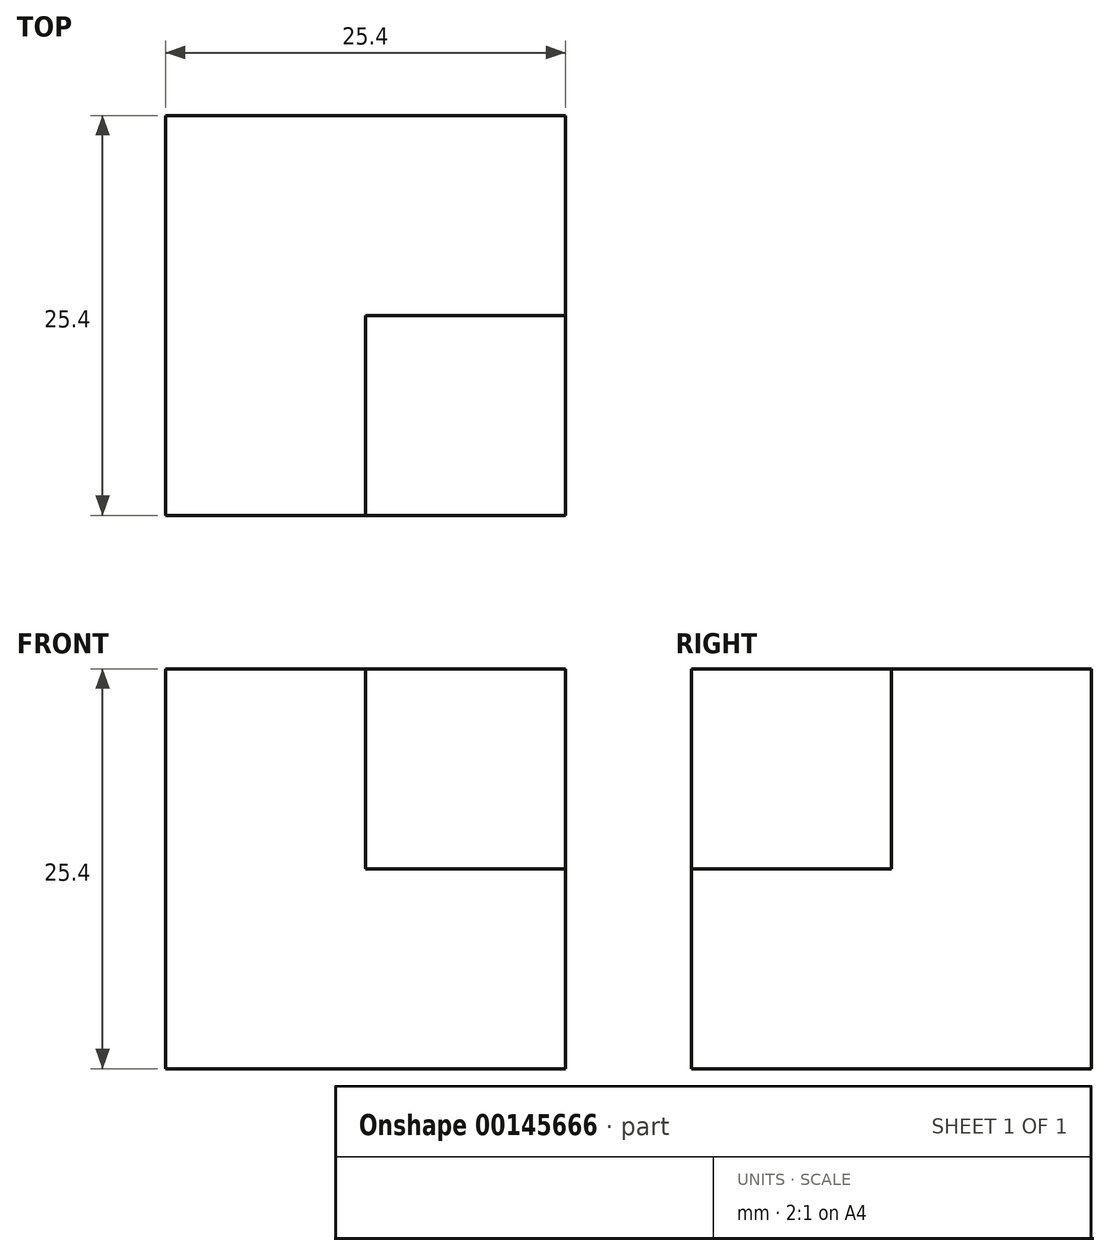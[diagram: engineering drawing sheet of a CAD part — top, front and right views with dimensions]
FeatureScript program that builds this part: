
annotation { "Feature Type Name" : "Feature", "Feature Type Description" : "" }
export const myFeature = defineFeature(function(context is Context, id is Id, definition is map)
    precondition{}
    {
        {
            var Q0;
            Q0=qCreatedBy(makeId("Top.planeOp"),FACE);
            var sketch = newSketch(context, id + "F0", { "sketchPlane" : qUnion([Q0])});
            skLineSegment(sketch, "E0.bottom", {"start": v(12.7, -12.7) * mm, "end": v(-12.7, -12.7) * mm});
            skLineSegment(sketch, "E0.top", {"start": v(12.7, 12.7) * mm, "end": v(-12.7, 12.7) * mm});
            skLineSegment(sketch, "E0.left", {"start": v(12.7, -12.7) * mm, "end": v(12.7, 12.7) * mm});
            skLineSegment(sketch, "E0.right", {"start": v(-12.7, -12.7) * mm, "end": v(-12.7, 12.7) * mm});
            skPoint(sketch, "E0.middle", {"position": v(0, 0) * mm});
            skSolve(sketch);
        }
        {
            var Q0;
            Q0 = qSketchRegion(id + "F0", true);
            extrude(context, id + "F1", {"entities" : qUnion([Q0]), "endBound" : BoundingType.SYMMETRIC, "depth" : 25.4 * mm});
        }
        {
            var Q0;
            Q0=makeQuery(id+"F1.opExtrude","CAP_FACE",FACE,{"disambiguationData":[OSD([sQuery(id+"F0.wireOp",EDGE,"E0.bottom"),sQuery(id+"F0.wireOp",EDGE,"E0.top"),sQuery(id+"F0.wireOp",EDGE,"E0.left"),sQuery(id+"F0.wireOp",EDGE,"E0.right")])],"isStart":false});
            var sketch = newSketch(context, id + "F2", { "sketchPlane" : qUnion([Q0])});
            skLineSegment(sketch, "E1.bottom", {"start": v(12.7, -12.7) * mm, "end": v(0, -12.7) * mm});
            skLineSegment(sketch, "E1.top", {"start": v(12.7, 0) * mm, "end": v(0, 0) * mm});
            skLineSegment(sketch, "E1.left", {"start": v(12.7, -12.7) * mm, "end": v(12.7, 0) * mm});
            skLineSegment(sketch, "E1.right", {"start": v(0, -12.7) * mm, "end": v(0, 0) * mm});
            skSolve(sketch);
        }
        {
            var Q0;
            Q0 = qSketchRegion(id + "F2", true);
            extrude(context, id + "F3", {"entities" : qUnion([Q0]), "operationType" : NewBodyOperationType.REMOVE, "oppositeDirection" : true, "depth" : 12.7 * mm});
        }
    });
